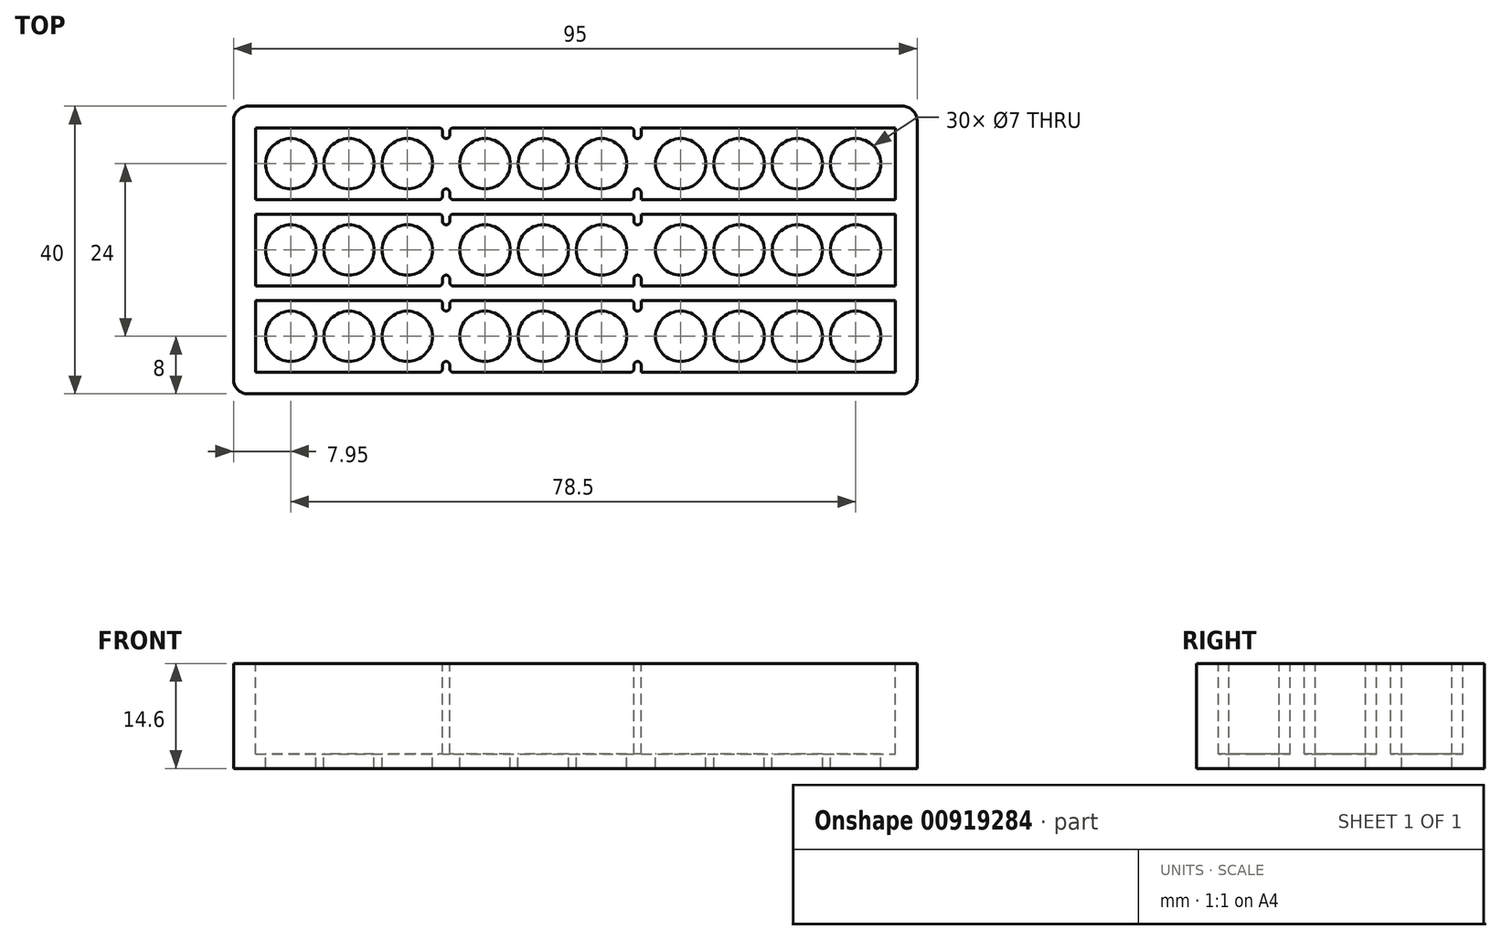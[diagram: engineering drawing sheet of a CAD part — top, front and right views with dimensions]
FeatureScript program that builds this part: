
annotation { "Feature Type Name" : "Feature", "Feature Type Description" : "" }
export const myFeature = defineFeature(function(context is Context, id is Id, definition is map)
    precondition{}
    {
        {
            var Q0;
            Q0=qCreatedBy(makeId("Top.planeOp"),FACE);
            var sketch = newSketch(context, id + "F0", { "sketchPlane" : qUnion([Q0])});
            skLineSegment(sketch, "E0.bottom", {"start": v(47.5, -20) * mm, "end": v(-47.5, -20) * mm});
            skLineSegment(sketch, "E0.top", {"start": v(47.5, 20) * mm, "end": v(-47.5, 20) * mm});
            skLineSegment(sketch, "E0.left", {"start": v(47.5, -20) * mm, "end": v(47.5, 20) * mm});
            skLineSegment(sketch, "E0.right", {"start": v(-47.5, -20) * mm, "end": v(-47.5, 20) * mm});
            skPoint(sketch, "E0.middle", {"position": v(0, 0) * mm});
            skSolve(sketch);
        }
        {
            var Q0;
            Q0=makeQuery(id+"F0.imprint","IMPRINT",FACE,{"disambiguationData":[TD([[makeQuery(id+"F0.imprint","IMPRINT",EDGE,{"derivedFrom":sQuery(id+"F0.wireOp",EDGE,"E0.bottom")}),-1.0]])]});
            extrude(context, id + "F1", {"entities" : qUnion([Q0]), "depth" : 14.6 * mm, "offsetDistance" : 25 * mm});
        }
        {
            var Q0;
            Q0=makeQuery(id+"F1.opExtrude","CAP_FACE",FACE,{"disambiguationData":[OSD([sQuery(id+"F0.wireOp",EDGE,"E0.bottom"),sQuery(id+"F0.wireOp",EDGE,"E0.top"),sQuery(id+"F0.wireOp",EDGE,"E0.left"),sQuery(id+"F0.wireOp",EDGE,"E0.right")])],"isStart":false});
            var sketch = newSketch(context, id + "F2", { "sketchPlane" : qUnion([Q0])});
            skLineSegment(sketch, "E1.bottom", {"start": v(-44.45, 17) * mm, "end": v(44.45, 17) * mm});
            skLineSegment(sketch, "E1.top", {"start": v(-44.45, 7) * mm, "end": v(44.45, 7) * mm});
            skLineSegment(sketch, "E1.left", {"start": v(-44.45, 17) * mm, "end": v(-44.45, 7) * mm});
            skLineSegment(sketch, "E1.right", {"start": v(44.45, 17) * mm, "end": v(44.45, 7) * mm});
            skLineSegment(sketch, "E2.bottom", {"start": v(-44.45, 5) * mm, "end": v(44.45, 5) * mm});
            skLineSegment(sketch, "E2.top", {"start": v(-44.45, -5) * mm, "end": v(44.45, -5) * mm});
            skLineSegment(sketch, "E2.left", {"start": v(-44.45, 5) * mm, "end": v(-44.45, -5) * mm});
            skLineSegment(sketch, "E2.right", {"start": v(44.45, 5) * mm, "end": v(44.45, -5) * mm});
            skLineSegment(sketch, "E3.bottom", {"start": v(-44.45, -7) * mm, "end": v(44.45, -7) * mm});
            skLineSegment(sketch, "E3.top", {"start": v(-44.45, -17) * mm, "end": v(44.45, -17) * mm});
            skLineSegment(sketch, "E3.left", {"start": v(-44.45, -7) * mm, "end": v(-44.45, -17) * mm});
            skLineSegment(sketch, "E3.right", {"start": v(44.45, -7) * mm, "end": v(44.45, -17) * mm});
            skLineSegment(sketch, "E4", {"start": v(-44.45, 0) * mm, "end": v(0, 0) * mm, "construction": true});
            skLineSegment(sketch, "E5", {"start": v(0, 0) * mm, "end": v(0, 5) * mm, "construction": true});
            skSolve(sketch);
        }
        {
            var Q0;
            Q0 = qSketchRegion(id + "F2", true);
            extrude(context, id + "F3", {"entities" : qUnion([Q0]), "operationType" : NewBodyOperationType.REMOVE, "oppositeDirection" : true, "depth" : 12.6 * mm, "offsetDistance" : 25 * mm});
        }
        {
            var Q0;
            Q0=makeQuery(id+"F1.opExtrude","CAP_FACE",FACE,{"disambiguationData":[OSD([sQuery(id+"F0.wireOp",EDGE,"E0.bottom"),sQuery(id+"F0.wireOp",EDGE,"E0.top"),sQuery(id+"F0.wireOp",EDGE,"E0.left"),sQuery(id+"F0.wireOp",EDGE,"E0.right")])],"isStart":false});
            var sketch = newSketch(context, id + "F4", { "sketchPlane" : qUnion([Q0])});
            skLineSegment(sketch, "E6.bottom", {"start": v(-18.45, 17) * mm, "end": v(-17.45, 17) * mm});
            skLineSegment(sketch, "E6.top", {"start": v(-18.45, 15.5) * mm, "end": v(-17.45, 15.5) * mm});
            skLineSegment(sketch, "E6.left", {"start": v(-18.45, 17) * mm, "end": v(-18.45, 15.5) * mm});
            skLineSegment(sketch, "E6.right", {"start": v(-17.45, 17) * mm, "end": v(-17.45, 15.5) * mm});
            skLineSegment(sketch, "E7.bottom", {"start": v(8.15, 17) * mm, "end": v(9.15, 17) * mm});
            skLineSegment(sketch, "E7.top", {"start": v(8.15, 15.5) * mm, "end": v(9.15, 15.5) * mm});
            skLineSegment(sketch, "E7.left", {"start": v(8.15, 17) * mm, "end": v(8.15, 15.5) * mm});
            skLineSegment(sketch, "E7.right", {"start": v(9.15, 17) * mm, "end": v(9.15, 15.5) * mm});
            skLineSegment(sketch, "E8", {"start": v(-44.45, 12) * mm, "end": v(44.45, 12) * mm, "construction": true});
            skLineSegment(sketch, "E9.MirrorCS", {"start": v(9.15, 7) * mm, "end": v(9.15, 8.5) * mm});
            skLineSegment(sketch, "E10.MirrorCS", {"start": v(-18.45, 7) * mm, "end": v(-17.45, 7) * mm});
            skLineSegment(sketch, "E11.MirrorCS", {"start": v(-18.45, 8.5) * mm, "end": v(-17.45, 8.5) * mm});
            skLineSegment(sketch, "E12.MirrorCS", {"start": v(-17.45, 7) * mm, "end": v(-17.45, 8.5) * mm});
            skLineSegment(sketch, "E13.MirrorCS", {"start": v(8.15, 8.5) * mm, "end": v(9.15, 8.5) * mm});
            skLineSegment(sketch, "E14.MirrorCS", {"start": v(8.15, 7) * mm, "end": v(8.15, 8.5) * mm});
            skLineSegment(sketch, "E15.MirrorCS", {"start": v(-18.45, 7) * mm, "end": v(-18.45, 8.5) * mm});
            skLineSegment(sketch, "E16.MirrorCS", {"start": v(8.15, 7) * mm, "end": v(9.15, 7) * mm});
            skLineSegment(sketch, "E17", {"start": v(-44.45, 7) * mm, "end": v(-44.45, 5) * mm, "construction": true});
            skLineSegment(sketch, "E18", {"start": v(-44.45, 6) * mm, "end": v(47.5, 6) * mm, "construction": true});
            skLineSegment(sketch, "E19.MirrorCS", {"start": v(-18.45, 5) * mm, "end": v(-17.45, 5) * mm});
            skLineSegment(sketch, "E20.MirrorCS", {"start": v(8.15, 5) * mm, "end": v(9.15, 5) * mm});
            skLineSegment(sketch, "E21.MirrorCS", {"start": v(8.15, 3.5) * mm, "end": v(9.15, 3.5) * mm});
            skLineSegment(sketch, "E22.MirrorCS", {"start": v(-18.45, 3.5) * mm, "end": v(-17.45, 3.5) * mm});
            skLineSegment(sketch, "E23.MirrorCS", {"start": v(8.15, 5) * mm, "end": v(8.15, 3.5) * mm});
            skLineSegment(sketch, "E24.MirrorCS", {"start": v(-17.45, 5) * mm, "end": v(-17.45, 3.5) * mm});
            skLineSegment(sketch, "E25.MirrorCS", {"start": v(9.15, 5) * mm, "end": v(9.15, 3.5) * mm});
            skLineSegment(sketch, "E26.MirrorCS", {"start": v(-18.45, 5) * mm, "end": v(-18.45, 3.5) * mm});
            skLineSegment(sketch, "E27", {"start": v(-44.45, 0) * mm, "end": v(0, 0) * mm, "construction": true});
            skLineSegment(sketch, "E28.MirrorCS", {"start": v(8.15, -17) * mm, "end": v(9.15, -17) * mm});
            skLineSegment(sketch, "E29.MirrorCS", {"start": v(-18.45, -17) * mm, "end": v(-17.45, -17) * mm});
            skLineSegment(sketch, "E30.MirrorCS", {"start": v(-18.45, -17) * mm, "end": v(-18.45, -15.5) * mm});
            skLineSegment(sketch, "E31.MirrorCS", {"start": v(-17.45, -17) * mm, "end": v(-17.45, -15.5) * mm});
            skLineSegment(sketch, "E32.MirrorCS", {"start": v(8.15, -15.5) * mm, "end": v(9.15, -15.5) * mm});
            skLineSegment(sketch, "E33.MirrorCS", {"start": v(-18.45, -15.5) * mm, "end": v(-17.45, -15.5) * mm});
            skLineSegment(sketch, "E34.MirrorCS", {"start": v(8.15, -17) * mm, "end": v(8.15, -15.5) * mm});
            skLineSegment(sketch, "E35.MirrorCS", {"start": v(9.15, -17) * mm, "end": v(9.15, -15.5) * mm});
            skLineSegment(sketch, "E36.MirrorCS", {"start": v(-18.45, -5) * mm, "end": v(-17.45, -5) * mm});
            skLineSegment(sketch, "E37.MirrorCS", {"start": v(-17.45, -7) * mm, "end": v(-17.45, -8.5) * mm});
            skLineSegment(sketch, "E38.MirrorCS", {"start": v(8.15, -3.5) * mm, "end": v(9.15, -3.5) * mm});
            skLineSegment(sketch, "E39.MirrorCS", {"start": v(9.15, -7) * mm, "end": v(9.15, -8.5) * mm});
            skLineSegment(sketch, "E40.MirrorCS", {"start": v(-18.45, -7) * mm, "end": v(-18.45, -8.5) * mm});
            skLineSegment(sketch, "E41.MirrorCS", {"start": v(-18.45, -5) * mm, "end": v(-18.45, -3.5) * mm});
            skLineSegment(sketch, "E42.MirrorCS", {"start": v(-18.45, -3.5) * mm, "end": v(-17.45, -3.5) * mm});
            skLineSegment(sketch, "E43.MirrorCS", {"start": v(8.15, -8.5) * mm, "end": v(9.15, -8.5) * mm});
            skLineSegment(sketch, "E44.MirrorCS", {"start": v(9.15, -5) * mm, "end": v(9.15, -3.5) * mm});
            skLineSegment(sketch, "E45.MirrorCS", {"start": v(8.15, -7) * mm, "end": v(9.15, -7) * mm});
            skLineSegment(sketch, "E46.MirrorCS", {"start": v(-17.45, -5) * mm, "end": v(-17.45, -3.5) * mm});
            skLineSegment(sketch, "E47.MirrorCS", {"start": v(-18.45, -8.5) * mm, "end": v(-17.45, -8.5) * mm});
            skLineSegment(sketch, "E48.MirrorCS", {"start": v(8.15, -5) * mm, "end": v(9.15, -5) * mm});
            skLineSegment(sketch, "E49.MirrorCS", {"start": v(8.15, -7) * mm, "end": v(8.15, -8.5) * mm});
            skLineSegment(sketch, "E50.MirrorCS", {"start": v(8.15, -5) * mm, "end": v(8.15, -3.5) * mm});
            skLineSegment(sketch, "E51.MirrorCS", {"start": v(-18.45, -7) * mm, "end": v(-17.45, -7) * mm});
            skSolve(sketch);
        }
        {
            var Q0;
            Q0 = qSketchRegion(id + "F4", true);
            extrude(context, id + "F5", {"entities" : qUnion([Q0]), "operationType" : NewBodyOperationType.ADD, "endBound" : BoundingType.UP_TO_NEXT, "oppositeDirection" : true, "depth" : 25 * mm, "offsetDistance" : 25 * mm});
        }
        {
            var Q0;
            Q0=makeQuery(id+"F4.imprint","IMPRINT",FACE,{"disambiguationData":[TD([[makeQuery(id+"F4.imprint","IMPRINT",EDGE,{"derivedFrom":sQuery(id+"F4.wireOp",EDGE,"E6.top")}),-1.0]])]});
            var sketch = newSketch(context, id + "F6", { "sketchPlane" : qUnion([Q0])});
            skCircle(sketch, "E52", {"center": v(-39.55, 12) * mm, "radius": 3.5 * mm});
            skCircle(sketch, "E53.1.0.0", {"center": v(-31.45, 12) * mm, "radius": 3.5 * mm});
            skCircle(sketch, "E53.2.0.0", {"center": v(-23.35, 12) * mm, "radius": 3.5 * mm});
            skLineSegment(sketch, "E53.direction1", {"start": v(-39.55, 12) * mm, "end": v(-31.45, 12) * mm, "construction": true});
            skCircle(sketch, "E54", {"center": v(-12.55, 12) * mm, "radius": 3.5 * mm});
            skCircle(sketch, "E55.1.0.0", {"center": v(-4.45, 12) * mm, "radius": 3.5 * mm});
            skCircle(sketch, "E55.2.0.0", {"center": v(3.65, 12) * mm, "radius": 3.5 * mm});
            skLineSegment(sketch, "E55.direction1", {"start": v(-12.55, 12) * mm, "end": v(-4.45, 12) * mm, "construction": true});
            skCircle(sketch, "E56", {"center": v(14.65, 12) * mm, "radius": 3.5 * mm});
            skLineSegment(sketch, "E57", {"start": v(-39.55, 12) * mm, "end": v(-44.45, 12) * mm, "construction": true});
            skLineSegment(sketch, "E58", {"start": v(-23.35, 12) * mm, "end": v(-18.45, 12) * mm, "construction": true});
            skLineSegment(sketch, "E59", {"start": v(-18.45, 12) * mm, "end": v(-18.45, 15.5) * mm, "construction": true});
            skCircle(sketch, "E60.1.0.0", {"center": v(22.75, 12) * mm, "radius": 3.5 * mm});
            skCircle(sketch, "E60.2.0.0", {"center": v(30.85, 12) * mm, "radius": 3.5 * mm});
            skCircle(sketch, "E60.3.0.0", {"center": v(38.95, 12) * mm, "radius": 3.5 * mm});
            skLineSegment(sketch, "E60.direction1", {"start": v(14.65, 12) * mm, "end": v(22.75, 12) * mm, "construction": true});
            skLineSegment(sketch, "E61", {"start": v(9.15, 15.5) * mm, "end": v(9.15, 12) * mm, "construction": true});
            skLineSegment(sketch, "E62", {"start": v(9.15, 12) * mm, "end": v(14.65, 12) * mm, "construction": true});
            skLineSegment(sketch, "E63", {"start": v(38.95, 12) * mm, "end": v(44.45, 12) * mm, "construction": true});
            skCircle(sketch, "E64.0.1.0", {"center": v(-39.55, 0) * mm, "radius": 3.5 * mm});
            skCircle(sketch, "E64.0.1.1", {"center": v(-31.45, 0) * mm, "radius": 3.5 * mm});
            skCircle(sketch, "E64.0.1.2", {"center": v(-23.35, 0) * mm, "radius": 3.5 * mm});
            skCircle(sketch, "E64.0.1.3", {"center": v(-12.55, 0) * mm, "radius": 3.5 * mm});
            skCircle(sketch, "E64.0.1.4", {"center": v(-4.45, 0) * mm, "radius": 3.5 * mm});
            skCircle(sketch, "E64.0.1.5", {"center": v(3.65, 0) * mm, "radius": 3.5 * mm});
            skCircle(sketch, "E64.0.1.6", {"center": v(14.65, 0) * mm, "radius": 3.5 * mm});
            skCircle(sketch, "E64.0.1.7", {"center": v(22.75, 0) * mm, "radius": 3.5 * mm});
            skCircle(sketch, "E64.0.1.8", {"center": v(30.85, 0) * mm, "radius": 3.5 * mm});
            skCircle(sketch, "E64.0.1.9", {"center": v(38.95, 0) * mm, "radius": 3.5 * mm});
            skCircle(sketch, "E64.0.2.0", {"center": v(-39.55, -12) * mm, "radius": 3.5 * mm});
            skCircle(sketch, "E64.0.2.1", {"center": v(-31.45, -12) * mm, "radius": 3.5 * mm});
            skCircle(sketch, "E64.0.2.2", {"center": v(-23.35, -12) * mm, "radius": 3.5 * mm});
            skCircle(sketch, "E64.0.2.3", {"center": v(-12.55, -12) * mm, "radius": 3.5 * mm});
            skCircle(sketch, "E64.0.2.4", {"center": v(-4.45, -12) * mm, "radius": 3.5 * mm});
            skCircle(sketch, "E64.0.2.5", {"center": v(3.65, -12) * mm, "radius": 3.5 * mm});
            skCircle(sketch, "E64.0.2.6", {"center": v(14.65, -12) * mm, "radius": 3.5 * mm});
            skCircle(sketch, "E64.0.2.7", {"center": v(22.75, -12) * mm, "radius": 3.5 * mm});
            skCircle(sketch, "E64.0.2.8", {"center": v(30.85, -12) * mm, "radius": 3.5 * mm});
            skCircle(sketch, "E64.0.2.9", {"center": v(38.95, -12) * mm, "radius": 3.5 * mm});
            skLineSegment(sketch, "E64.direction1", {"start": v(-39.55, 12) * mm, "end": v(-14.55, 12) * mm, "construction": true});
            skLineSegment(sketch, "E64.direction2", {"start": v(-39.55, 12) * mm, "end": v(-39.55, 0) * mm, "construction": true});
            skSolve(sketch);
        }
        {
            var Q0;
            Q0 = qSketchRegion(id + "F6", true);
            extrude(context, id + "F7", {"entities" : qUnion([Q0]), "operationType" : NewBodyOperationType.REMOVE, "endBound" : BoundingType.THROUGH_ALL, "oppositeDirection" : true, "depth" : 25 * mm, "offsetDistance" : 25 * mm});
        }
        {
            var Q0;
            Q0=makeQuery(id+"F1.opExtrude","SWEPT_EDGE",EDGE,{"disambiguationData":[OSD([sQuery(id+"F0.wireOp",EDGE,"E0.bottom"),sQuery(id+"F0.wireOp",EDGE,"E0.right")])]});
            var Q1;
            Q1=makeQuery(id+"F1.opExtrude","SWEPT_EDGE",EDGE,{"disambiguationData":[OSD([sQuery(id+"F0.wireOp",EDGE,"E0.bottom"),sQuery(id+"F0.wireOp",EDGE,"E0.left")])]});
            var Q2;
            Q2=makeQuery(id+"F1.opExtrude","SWEPT_EDGE",EDGE,{"disambiguationData":[OSD([sQuery(id+"F0.wireOp",EDGE,"E0.top"),sQuery(id+"F0.wireOp",EDGE,"E0.left")])]});
            var Q3;
            Q3=makeQuery(id+"F1.opExtrude","SWEPT_EDGE",EDGE,{"disambiguationData":[OSD([sQuery(id+"F0.wireOp",EDGE,"E0.top"),sQuery(id+"F0.wireOp",EDGE,"E0.right")])]});
            fillet(context, id + "F8", {"entities" : qUnion([Q0, Q1, Q2, Q3]), "radius" : 2 * mm, "tangentPropagation" : true, "allowEdgeOverflow" : false});
        }
        {
            var Q0;
            Q0=makeQuery(id+"F5.opExtrude","SWEPT_EDGE",EDGE,{"disambiguationData":[OSD([sQuery(id+"F2.wireOp",EDGE,"E1.bottom"),sQuery(id+"F4.wireOp",EDGE,"E6.bottom"),sQuery(id+"F4.wireOp",EDGE,"E6.left")])]});
            var Q1;
            Q1=makeQuery(id+"F5.opExtrude","SWEPT_EDGE",EDGE,{"disambiguationData":[OSD([sQuery(id+"F4.wireOp",EDGE,"E6.top"),sQuery(id+"F4.wireOp",EDGE,"E6.left")])]});
            var Q2;
            Q2=makeQuery(id+"F5.opExtrude","SWEPT_EDGE",EDGE,{"disambiguationData":[OSD([sQuery(id+"F4.wireOp",EDGE,"E6.top"),sQuery(id+"F4.wireOp",EDGE,"E6.right")])]});
            var Q3;
            Q3=makeQuery(id+"F5.opExtrude","SWEPT_EDGE",EDGE,{"disambiguationData":[OSD([sQuery(id+"F2.wireOp",EDGE,"E1.bottom"),sQuery(id+"F4.wireOp",EDGE,"E7.bottom"),sQuery(id+"F4.wireOp",EDGE,"E7.left")])]});
            var Q4;
            Q4=makeQuery(id+"F5.opExtrude","SWEPT_EDGE",EDGE,{"disambiguationData":[OSD([sQuery(id+"F4.wireOp",EDGE,"E7.top"),sQuery(id+"F4.wireOp",EDGE,"E7.left")])]});
            var Q5;
            Q5=makeQuery(id+"F5.opExtrude","SWEPT_EDGE",EDGE,{"disambiguationData":[OSD([sQuery(id+"F4.wireOp",EDGE,"E7.top"),sQuery(id+"F4.wireOp",EDGE,"E7.right")])]});
            var Q6;
            Q6=makeQuery(id+"F5.opExtrude","SWEPT_EDGE",EDGE,{"disambiguationData":[OSD([sQuery(id+"F4.wireOp",EDGE,"E13.MirrorCS"),sQuery(id+"F4.wireOp",EDGE,"E14.MirrorCS")])]});
            var Q7;
            Q7=makeQuery(id+"F5.opExtrude","SWEPT_EDGE",EDGE,{"disambiguationData":[OSD([sQuery(id+"F4.wireOp",EDGE,"E11.MirrorCS"),sQuery(id+"F4.wireOp",EDGE,"E15.MirrorCS")])]});
            var Q8;
            Q8=makeQuery(id+"F5.opExtrude","SWEPT_EDGE",EDGE,{"disambiguationData":[OSD([sQuery(id+"F2.wireOp",EDGE,"E2.bottom"),sQuery(id+"F4.wireOp",EDGE,"E19.MirrorCS"),sQuery(id+"F4.wireOp",EDGE,"E26.MirrorCS")])]});
            var Q9;
            Q9=makeQuery(id+"F5.opExtrude","SWEPT_EDGE",EDGE,{"disambiguationData":[OSD([sQuery(id+"F4.wireOp",EDGE,"E22.MirrorCS"),sQuery(id+"F4.wireOp",EDGE,"E26.MirrorCS")])]});
            var Q10;
            Q10=makeQuery(id+"F5.opExtrude","SWEPT_EDGE",EDGE,{"disambiguationData":[OSD([sQuery(id+"F4.wireOp",EDGE,"E22.MirrorCS"),sQuery(id+"F4.wireOp",EDGE,"E24.MirrorCS")])]});
            var Q11;
            Q11=makeQuery(id+"F5.opExtrude","SWEPT_EDGE",EDGE,{"disambiguationData":[OSD([sQuery(id+"F2.wireOp",EDGE,"E2.bottom"),sQuery(id+"F4.wireOp",EDGE,"E20.MirrorCS"),sQuery(id+"F4.wireOp",EDGE,"E23.MirrorCS")])]});
            var Q12;
            Q12=makeQuery(id+"F5.opExtrude","SWEPT_EDGE",EDGE,{"disambiguationData":[OSD([sQuery(id+"F4.wireOp",EDGE,"E21.MirrorCS"),sQuery(id+"F4.wireOp",EDGE,"E23.MirrorCS")])]});
            var Q13;
            Q13=makeQuery(id+"F5.opExtrude","SWEPT_EDGE",EDGE,{"disambiguationData":[OSD([sQuery(id+"F4.wireOp",EDGE,"E41.MirrorCS"),sQuery(id+"F4.wireOp",EDGE,"E42.MirrorCS")])]});
            var Q14;
            Q14=makeQuery(id+"F5.opExtrude","SWEPT_EDGE",EDGE,{"disambiguationData":[OSD([sQuery(id+"F4.wireOp",EDGE,"E38.MirrorCS"),sQuery(id+"F4.wireOp",EDGE,"E50.MirrorCS")])]});
            var Q15;
            Q15=makeQuery(id+"F5.opExtrude","SWEPT_EDGE",EDGE,{"disambiguationData":[OSD([sQuery(id+"F4.wireOp",EDGE,"E40.MirrorCS"),sQuery(id+"F4.wireOp",EDGE,"E47.MirrorCS")])]});
            var Q16;
            Q16=makeQuery(id+"F5.opExtrude","SWEPT_EDGE",EDGE,{"disambiguationData":[OSD([sQuery(id+"F4.wireOp",EDGE,"E37.MirrorCS"),sQuery(id+"F4.wireOp",EDGE,"E47.MirrorCS")])]});
            var Q17;
            Q17=makeQuery(id+"F5.opExtrude","SWEPT_EDGE",EDGE,{"disambiguationData":[OSD([sQuery(id+"F2.wireOp",EDGE,"E3.bottom"),sQuery(id+"F4.wireOp",EDGE,"E40.MirrorCS"),sQuery(id+"F4.wireOp",EDGE,"E51.MirrorCS")])]});
            var Q18;
            Q18=makeQuery(id+"F5.opExtrude","SWEPT_EDGE",EDGE,{"disambiguationData":[OSD([sQuery(id+"F2.wireOp",EDGE,"E3.bottom"),sQuery(id+"F4.wireOp",EDGE,"E45.MirrorCS"),sQuery(id+"F4.wireOp",EDGE,"E49.MirrorCS")])]});
            var Q19;
            Q19=makeQuery(id+"F5.opExtrude","SWEPT_EDGE",EDGE,{"disambiguationData":[OSD([sQuery(id+"F4.wireOp",EDGE,"E43.MirrorCS"),sQuery(id+"F4.wireOp",EDGE,"E49.MirrorCS")])]});
            var Q20;
            Q20=makeQuery(id+"F5.opExtrude","SWEPT_EDGE",EDGE,{"disambiguationData":[OSD([sQuery(id+"F4.wireOp",EDGE,"E39.MirrorCS"),sQuery(id+"F4.wireOp",EDGE,"E43.MirrorCS")])]});
            var Q21;
            Q21=makeQuery(id+"F5.opExtrude","SWEPT_EDGE",EDGE,{"disambiguationData":[OSD([sQuery(id+"F4.wireOp",EDGE,"E32.MirrorCS"),sQuery(id+"F4.wireOp",EDGE,"E34.MirrorCS")])]});
            var Q22;
            Q22=makeQuery(id+"F5.opExtrude","SWEPT_EDGE",EDGE,{"disambiguationData":[OSD([sQuery(id+"F4.wireOp",EDGE,"E30.MirrorCS"),sQuery(id+"F4.wireOp",EDGE,"E33.MirrorCS")])]});
            var Q23;
            Q23=makeQuery(id+"F5.opExtrude","SWEPT_EDGE",EDGE,{"disambiguationData":[OSD([sQuery(id+"F2.wireOp",EDGE,"E3.top"),sQuery(id+"F4.wireOp",EDGE,"E29.MirrorCS"),sQuery(id+"F4.wireOp",EDGE,"E31.MirrorCS")])]});
            var Q24;
            Q24=makeQuery(id+"F5.opExtrude","SWEPT_EDGE",EDGE,{"disambiguationData":[OSD([sQuery(id+"F4.wireOp",EDGE,"E31.MirrorCS"),sQuery(id+"F4.wireOp",EDGE,"E33.MirrorCS")])]});
            var Q25;
            Q25=makeQuery(id+"F5.opExtrude","SWEPT_EDGE",EDGE,{"disambiguationData":[OSD([sQuery(id+"F2.wireOp",EDGE,"E3.top"),sQuery(id+"F4.wireOp",EDGE,"E28.MirrorCS"),sQuery(id+"F4.wireOp",EDGE,"E35.MirrorCS")])]});
            var Q26;
            Q26=makeQuery(id+"F5.opExtrude","SWEPT_EDGE",EDGE,{"disambiguationData":[OSD([sQuery(id+"F4.wireOp",EDGE,"E32.MirrorCS"),sQuery(id+"F4.wireOp",EDGE,"E35.MirrorCS")])]});
            var Q27;
            Q27=makeQuery(id+"F5.opExtrude","SWEPT_EDGE",EDGE,{"disambiguationData":[OSD([sQuery(id+"F2.wireOp",EDGE,"E2.top"),sQuery(id+"F4.wireOp",EDGE,"E44.MirrorCS"),sQuery(id+"F4.wireOp",EDGE,"E48.MirrorCS")])]});
            var Q28;
            Q28=makeQuery(id+"F5.opExtrude","SWEPT_EDGE",EDGE,{"disambiguationData":[OSD([sQuery(id+"F4.wireOp",EDGE,"E38.MirrorCS"),sQuery(id+"F4.wireOp",EDGE,"E44.MirrorCS")])]});
            var Q29;
            Q29=makeQuery(id+"F5.opExtrude","SWEPT_EDGE",EDGE,{"disambiguationData":[OSD([sQuery(id+"F4.wireOp",EDGE,"E9.MirrorCS"),sQuery(id+"F4.wireOp",EDGE,"E13.MirrorCS")])]});
            var Q30;
            Q30=makeQuery(id+"F5.opExtrude","SWEPT_EDGE",EDGE,{"disambiguationData":[OSD([sQuery(id+"F4.wireOp",EDGE,"E21.MirrorCS"),sQuery(id+"F4.wireOp",EDGE,"E25.MirrorCS")])]});
            var Q31;
            Q31=makeQuery(id+"F5.opExtrude","SWEPT_EDGE",EDGE,{"disambiguationData":[OSD([sQuery(id+"F4.wireOp",EDGE,"E42.MirrorCS"),sQuery(id+"F4.wireOp",EDGE,"E46.MirrorCS")])]});
            var Q32;
            Q32=makeQuery(id+"F5.opExtrude","SWEPT_EDGE",EDGE,{"disambiguationData":[OSD([sQuery(id+"F2.wireOp",EDGE,"E2.top"),sQuery(id+"F4.wireOp",EDGE,"E36.MirrorCS"),sQuery(id+"F4.wireOp",EDGE,"E46.MirrorCS")])]});
            var Q33;
            Q33=makeQuery(id+"F5.opExtrude","SWEPT_EDGE",EDGE,{"disambiguationData":[OSD([sQuery(id+"F4.wireOp",EDGE,"E11.MirrorCS"),sQuery(id+"F4.wireOp",EDGE,"E12.MirrorCS")])]});
            var Q34;
            Q34=makeQuery(id+"F5.opExtrude","SWEPT_EDGE",EDGE,{"disambiguationData":[OSD([sQuery(id+"F2.wireOp",EDGE,"E1.top"),sQuery(id+"F4.wireOp",EDGE,"E10.MirrorCS"),sQuery(id+"F4.wireOp",EDGE,"E12.MirrorCS")])]});
            var Q35;
            Q35=makeQuery(id+"F5.opExtrude","SWEPT_EDGE",EDGE,{"disambiguationData":[OSD([sQuery(id+"F2.wireOp",EDGE,"E1.top"),sQuery(id+"F4.wireOp",EDGE,"E9.MirrorCS"),sQuery(id+"F4.wireOp",EDGE,"E16.MirrorCS")])]});
            var Q36;
            Q36=makeQuery(id+"F5.opExtrude","SWEPT_EDGE",EDGE,{"disambiguationData":[OSD([sQuery(id+"F2.wireOp",EDGE,"E3.top"),sQuery(id+"F4.wireOp",EDGE,"E28.MirrorCS"),sQuery(id+"F4.wireOp",EDGE,"E34.MirrorCS")])]});
            var Q37;
            Q37=makeQuery(id+"F5.opExtrude","SWEPT_EDGE",EDGE,{"disambiguationData":[OSD([sQuery(id+"F2.wireOp",EDGE,"E3.top"),sQuery(id+"F4.wireOp",EDGE,"E29.MirrorCS"),sQuery(id+"F4.wireOp",EDGE,"E30.MirrorCS")])]});
            var Q38;
            Q38=makeQuery(id+"F5.opExtrude","SWEPT_EDGE",EDGE,{"disambiguationData":[OSD([sQuery(id+"F2.wireOp",EDGE,"E2.top"),sQuery(id+"F4.wireOp",EDGE,"E36.MirrorCS"),sQuery(id+"F4.wireOp",EDGE,"E41.MirrorCS")])]});
            var Q39;
            Q39=makeQuery(id+"F5.opExtrude","SWEPT_EDGE",EDGE,{"disambiguationData":[OSD([sQuery(id+"F2.wireOp",EDGE,"E1.top"),sQuery(id+"F4.wireOp",EDGE,"E10.MirrorCS"),sQuery(id+"F4.wireOp",EDGE,"E15.MirrorCS")])]});
            var Q40;
            Q40=makeQuery(id+"F5.opExtrude","SWEPT_EDGE",EDGE,{"disambiguationData":[OSD([sQuery(id+"F2.wireOp",EDGE,"E1.top"),sQuery(id+"F4.wireOp",EDGE,"E14.MirrorCS"),sQuery(id+"F4.wireOp",EDGE,"E16.MirrorCS")])]});
            var Q41;
            Q41=makeQuery(id+"F5.opExtrude","SWEPT_EDGE",EDGE,{"disambiguationData":[OSD([sQuery(id+"F2.wireOp",EDGE,"E3.bottom"),sQuery(id+"F4.wireOp",EDGE,"E39.MirrorCS"),sQuery(id+"F4.wireOp",EDGE,"E45.MirrorCS")])]});
            var Q42;
            Q42=makeQuery(id+"F5.opExtrude","SWEPT_EDGE",EDGE,{"disambiguationData":[OSD([sQuery(id+"F2.wireOp",EDGE,"E2.bottom"),sQuery(id+"F4.wireOp",EDGE,"E20.MirrorCS"),sQuery(id+"F4.wireOp",EDGE,"E25.MirrorCS")])]});
            var Q43;
            Q43=makeQuery(id+"F5.opExtrude","SWEPT_EDGE",EDGE,{"disambiguationData":[OSD([sQuery(id+"F2.wireOp",EDGE,"E2.bottom"),sQuery(id+"F4.wireOp",EDGE,"E19.MirrorCS"),sQuery(id+"F4.wireOp",EDGE,"E24.MirrorCS")])]});
            var Q44;
            Q44=makeQuery(id+"F5.opExtrude","SWEPT_EDGE",EDGE,{"disambiguationData":[OSD([sQuery(id+"F2.wireOp",EDGE,"E3.bottom"),sQuery(id+"F4.wireOp",EDGE,"E37.MirrorCS"),sQuery(id+"F4.wireOp",EDGE,"E51.MirrorCS")])]});
            var Q45;
            Q45=makeQuery(id+"F5.opExtrude","SWEPT_EDGE",EDGE,{"disambiguationData":[OSD([sQuery(id+"F2.wireOp",EDGE,"E1.bottom"),sQuery(id+"F4.wireOp",EDGE,"E7.bottom"),sQuery(id+"F4.wireOp",EDGE,"E7.right")])]});
            var Q46;
            Q46=makeQuery(id+"F5.opExtrude","SWEPT_EDGE",EDGE,{"disambiguationData":[OSD([sQuery(id+"F2.wireOp",EDGE,"E1.bottom"),sQuery(id+"F4.wireOp",EDGE,"E6.bottom"),sQuery(id+"F4.wireOp",EDGE,"E6.right")])]});
            fillet(context, id + "F9", {"entities" : qUnion([Q0, Q1, Q2, Q3, Q4, Q5, Q6, Q7, Q8, Q9, Q10, Q11, Q12, Q13, Q14, Q15, Q16, Q17, Q18, Q19, Q20, Q21, Q22, Q23, Q24, Q25, Q26, Q27, Q28, Q29, Q30, Q31, Q32, Q33, Q34, Q35, Q36, Q37, Q38, Q39, Q40, Q41, Q42, Q43, Q44, Q45, Q46]), "radius" : .5 * mm, "tangentPropagation" : true, "allowEdgeOverflow" : false});
        }
    });
